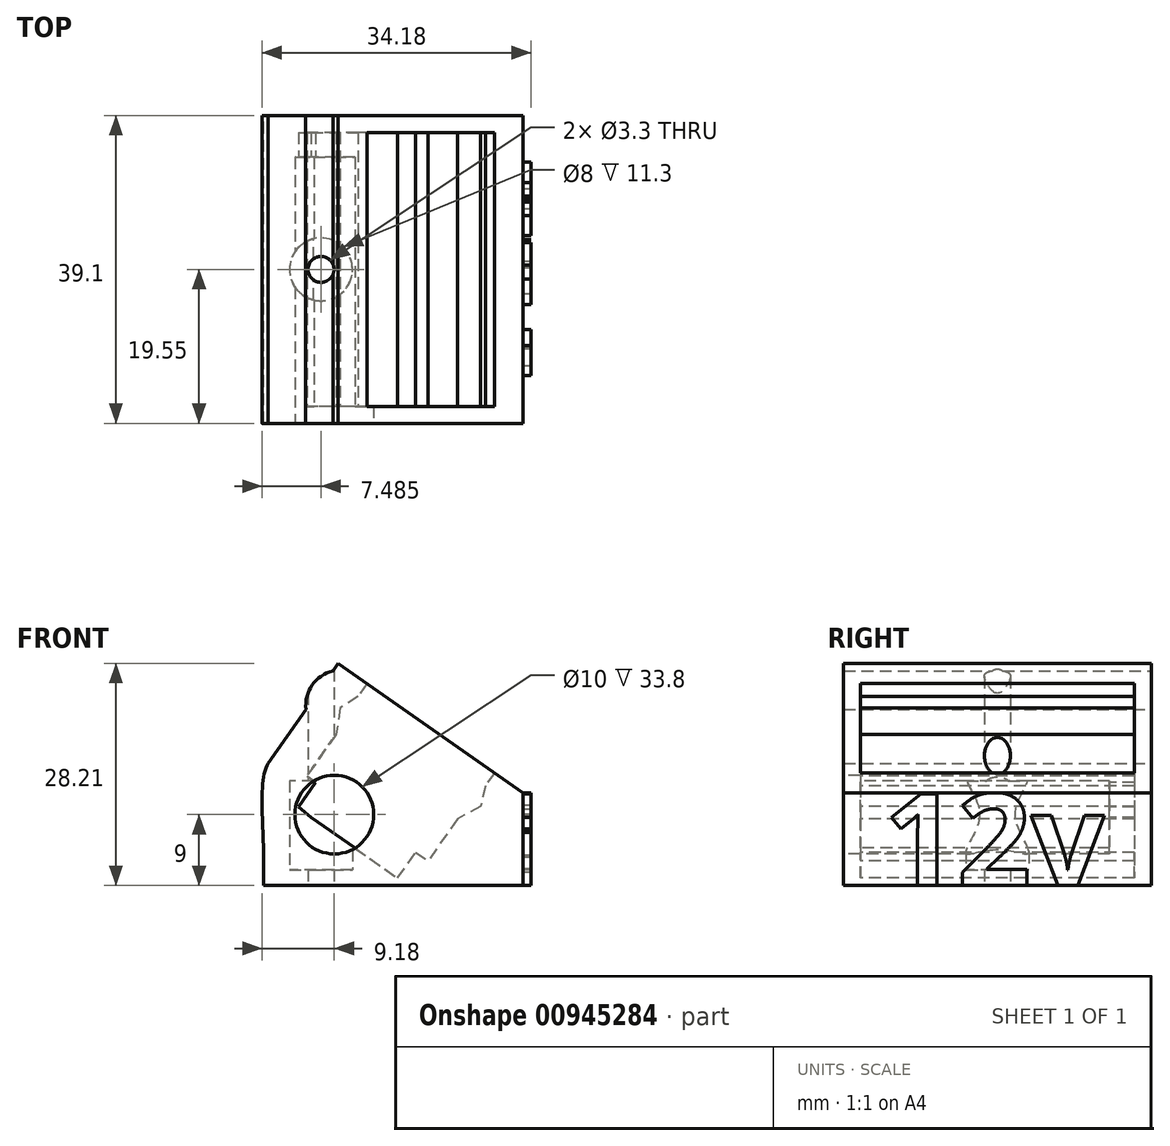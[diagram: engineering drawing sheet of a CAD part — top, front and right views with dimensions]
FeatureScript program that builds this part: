
annotation { "Feature Type Name" : "Feature", "Feature Type Description" : "" }
export const myFeature = defineFeature(function(context is Context, id is Id, definition is map)
    precondition{}
    {
        {
            var Q0;
            Q0=qCreatedBy(makeId("Front.planeOp"),FACE);
            var sketch = newSketch(context, id + "F0", { "sketchPlane" : qUnion([Q0])});
            skLineSegment(sketch, "E0.bottom", {"start": v(0, 0) * mm, "end": v(-33, 0) * mm});
            skLineSegment(sketch, "E0.top", {"start": v(0, 4) * mm, "end": v(-33, 4) * mm});
            skLineSegment(sketch, "E0.left", {"start": v(0, 0) * mm, "end": v(0, 4) * mm});
            skLineSegment(sketch, "E0.right", {"start": v(-33, 0) * mm, "end": v(-33, 4) * mm});
            skLineSegment(sketch, "E1", {"start": v(-30.88, 15.06) * mm, "end": v(-9.83, 0.32) * mm, "construction": true});
            skLineSegment(sketch, "E2", {"start": v(-9.83, 0.32) * mm, "end": v(-1.23, 12.6) * mm, "construction": true});
            skLineSegment(sketch, "E3", {"start": v(-1.23, 12.6) * mm, "end": v(0, 11.74) * mm, "construction": true});
            skLineSegment(sketch, "E4", {"start": v(-22.28, 27.35) * mm, "end": v(-30.88, 15.06) * mm, "construction": true});
            skLineSegment(sketch, "E5", {"start": v(0, 4) * mm, "end": v(0, 11.74) * mm});
            skLineSegment(sketch, "E6", {"start": v(-32.4, 15.5) * mm, "end": v(-15.96, 4) * mm});
            skLineSegment(sketch, "E7", {"start": v(0, 7.87) * mm, "end": v(13.32, 7.87) * mm});
            skLineSegment(sketch, "E8", {"start": v(13.32, 7.87) * mm, "end": v(13.32, 0) * mm});
            skLineSegment(sketch, "E9", {"start": v(13.32, 0) * mm, "end": v(0, 0) * mm});
            skLineSegment(sketch, "E10", {"start": v(21.82, 30.5) * mm, "end": v(-34.66, 30.5) * mm, "construction": true});
            skLineSegment(sketch, "E11", {"start": v(-22.28, 27.35) * mm, "end": v(-23.5, 28.2) * mm, "construction": true});
            skLineSegment(sketch, "E12", {"start": v(-23.5, 28.2) * mm, "end": v(-21.9, 30.5) * mm, "construction": true});
            skLineSegment(sketch, "E13", {"start": v(-21.9, 30.5) * mm, "end": v(1.6, 14.04) * mm, "construction": true});
            skLineSegment(sketch, "E14", {"start": v(0, 11.74) * mm, "end": v(1.6, 14.04) * mm, "construction": true});
            skLineSegment(sketch, "E15", {"start": v(-29.2, 13.88) * mm, "end": v(-31.73, 10.28) * mm, "construction": true});
            skLineSegment(sketch, "E16", {"start": v(-31.73, 10.28) * mm, "end": v(-14.04, -2.11) * mm, "construction": true});
            skLineSegment(sketch, "E17", {"start": v(-14.04, -2.11) * mm, "end": v(-11.51, 1.5) * mm, "construction": true});
            skLineSegment(sketch, "E18", {"start": v(-22.88, 4.08) * mm, "end": v(-20.36, 7.69) * mm, "construction": true});
            skLineSegment(sketch, "E19", {"start": v(0, 11.74) * mm, "end": v(-23.5, 28.2) * mm});
            skLineSegment(sketch, "E20", {"start": v(-23.5, 28.2) * mm, "end": v(-32.4, 15.5) * mm});
            skLineSegment(sketch, "E21", {"start": v(-1.1, 12.52) * mm, "end": v(-9.87, 0) * mm});
            skLineSegment(sketch, "E22", {"start": v(-22.4, 27.43) * mm, "end": v(-31.3, 14.74) * mm});
            skFitSpline(sketch, "E23", {"points": [v(-32.4, 15.5) * mm, v(-33, 4) * mm], "startDerivative": vector(-3.84, -5.87) * mm, "endDerivative": vector(0, -11.95) * mm});
            skLineSegment(sketch, "E24", {"start": v(-15.96, 4) * mm, "end": v(-10.25, 0) * mm});
            skLineSegment(sketch, "E25", {"start": v(-23.03, 26.54) * mm, "end": v(-25.92, 24.77) * mm});
            skLineSegment(sketch, "E26", {"start": v(-25.92, 24.77) * mm, "end": v(-26.47, 21.62) * mm});
            skLineSegment(sketch, "E27.MirrorCS", {"start": v(-1.73, 11.62) * mm, "end": v(-2.4, 8.3) * mm});
            skLineSegment(sketch, "E28.MirrorCS", {"start": v(-2.4, 8.3) * mm, "end": v(-5.17, 6.7) * mm});
            skArc(sketch, "E29", {"start": v(-24.18, 27.25) * mm, "mid": v(-26.8, 25.44) * mm, "end": v(-27.6, 22.35) * mm});
            skLineSegment(sketch, "E30", {"start": v(-23.25, 28.02) * mm, "end": v(-25.23, 25.19) * mm});
            skLineSegment(sketch, "E31.MirrorCS", {"start": v(-0.26, 11.93) * mm, "end": v(-2.25, 9.1) * mm});
            skLineSegment(sketch, "E32", {"start": v(-19.45, 25.37) * mm, "end": v(-27.48, 13.9) * mm});
            skLineSegment(sketch, "E33", {"start": v(-19.85, 25.64) * mm, "end": v(-21, 24) * mm});
            skLineSegment(sketch, "E34", {"start": v(-21, 24) * mm, "end": v(-23.26, 22.54) * mm});
            skLineSegment(sketch, "E35", {"start": v(-23.26, 22.54) * mm, "end": v(-23.77, 19.2) * mm});
            skLineSegment(sketch, "E36", {"start": v(-23.26, 22.54) * mm, "end": v(-22.04, 21.68) * mm});
            skLineSegment(sketch, "E37.MirrorCS", {"start": v(-4.05, 14.58) * mm, "end": v(-12.08, 3.12) * mm});
            skLineSegment(sketch, "E38.MirrorCS", {"start": v(-5.4, 10.04) * mm, "end": v(-8.37, 8.42) * mm});
            skLineSegment(sketch, "E39.MirrorCS", {"start": v(-4.8, 12.67) * mm, "end": v(-5.4, 10.04) * mm});
            skLineSegment(sketch, "E40.MirrorCS", {"start": v(-3.66, 14.3) * mm, "end": v(-4.8, 12.67) * mm});
            skLineSegment(sketch, "E41", {"start": v(-27.48, 13.9) * mm, "end": v(-12.08, 3.12) * mm});
            skLineSegment(sketch, "E42", {"start": v(-26.93, 8.63) * mm, "end": v(-18.27, 2.57) * mm});
            skLineSegment(sketch, "E43", {"start": v(-18.27, 2.57) * mm, "end": v(-15.95, 0.94) * mm});
            skLineSegment(sketch, "E44", {"start": v(-15.95, 0.94) * mm, "end": v(-13.66, 4.22) * mm});
            skLineSegment(sketch, "E45", {"start": v(-26.36, 13.11) * mm, "end": v(-28.56, 9.97) * mm});
            skLineSegment(sketch, "E46", {"start": v(-28.56, 9.97) * mm, "end": v(-26.93, 8.63) * mm});
            skSolve(sketch);
        }
        {
            var Q0;
            {var subQ6=sQuery(id+"F0.wireOp",EDGE,"E33");Q0=makeQuery(id+"F0.imprint","IMPRINT",FACE,{"disambiguationData":[TD([[makeQuery(id+"F0.imprint","IMPRINT",EDGE,{"derivedFrom":subQ6}),-1.0]])]});}
            var Q1;
            {var subQ3=sQuery(id+"F0.wireOp",EDGE,"E37.MirrorCS");var subQ4=sQuery(id+"F0.wireOp",EDGE,"E0.top");var subQ5=makeQuery(id+"F0.imprint","INTERSECT",VERTEX,{"derivedFrom":[subQ4,subQ3]});Q1=makeQuery(id+"F0.imprint","IMPRINT",FACE,{"disambiguationData":[TD([[makeQuery(id+"F0.imprint","IMPRINT",EDGE,{"disambiguationData":[TD([[subQ5,-1.0]])],"derivedFrom":subQ4}),-1.0]])]});}
            var Q2;
            {var subQ0=sQuery(id+"F0.wireOp",EDGE,"E38.MirrorCS");Q2=makeQuery(id+"F0.imprint","IMPRINT",FACE,{"disambiguationData":[TD([[makeQuery(id+"F0.imprint","IMPRINT",EDGE,{"derivedFrom":subQ0}),-1.0]])]});}
            var Q3;
            {var subQ10=sQuery(id+"F0.wireOp",EDGE,"E38.MirrorCS");Q3=makeQuery(id+"F0.imprint","IMPRINT",FACE,{"disambiguationData":[TD([[makeQuery(id+"F0.imprint","IMPRINT",EDGE,{"derivedFrom":subQ10}),1.0]])]});}
            var Q4;
            {var subQ7=sQuery(id+"F0.wireOp",EDGE,"E24");Q4=makeQuery(id+"F0.imprint","IMPRINT",FACE,{"disambiguationData":[TD([[makeQuery(id+"F0.imprint","IMPRINT",EDGE,{"derivedFrom":subQ7}),1.0]])]});}
            var Q5;
            {var subQ0=sQuery(id+"F0.wireOp",EDGE,"E37.MirrorCS");var subQ1=sQuery(id+"F0.wireOp",EDGE,"E0.top");var subQ2=makeQuery(id+"F0.imprint","INTERSECT",VERTEX,{"derivedFrom":[subQ1,subQ0]});Q5=makeQuery(id+"F0.imprint","IMPRINT",FACE,{"disambiguationData":[TD([[makeQuery(id+"F0.imprint","IMPRINT",EDGE,{"disambiguationData":[TD([[subQ2,-1.0]])],"derivedFrom":subQ1}),1.0]])]});}
            var Q6;
            {var subQ5=sQuery(id+"F0.wireOp",EDGE,"E28.MirrorCS");Q6=makeQuery(id+"F0.imprint","IMPRINT",FACE,{"disambiguationData":[TD([[makeQuery(id+"F0.imprint","IMPRINT",EDGE,{"derivedFrom":subQ5}),1.0]])]});}
            var Q7;
            {var subQ3=sQuery(id+"F0.wireOp",EDGE,"E28.MirrorCS");Q7=makeQuery(id+"F0.imprint","IMPRINT",FACE,{"disambiguationData":[TD([[makeQuery(id+"F0.imprint","IMPRINT",EDGE,{"derivedFrom":subQ3}),-1.0]])]});}
            var Q8;
            {var subQ3=sQuery(id+"F0.wireOp",EDGE,"E31.MirrorCS");Q8=makeQuery(id+"F0.imprint","IMPRINT",FACE,{"disambiguationData":[TD([[makeQuery(id+"F0.imprint","IMPRINT",EDGE,{"derivedFrom":subQ3}),-1.0]])]});}
            var Q9;
            {var subQ0=sQuery(id+"F0.wireOp",EDGE,"E0.left");Q9=makeQuery(id+"F0.imprint","IMPRINT",FACE,{"disambiguationData":[TD([[makeQuery(id+"F0.imprint","IMPRINT",EDGE,{"derivedFrom":subQ0}),1.0]])]});}
            var Q10;
            {var subQ0=sQuery(id+"F0.wireOp",EDGE,"E0.right");Q10=makeQuery(id+"F0.imprint","IMPRINT",FACE,{"disambiguationData":[TD([[makeQuery(id+"F0.imprint","IMPRINT",EDGE,{"derivedFrom":subQ0}),-1.0]])]});}
            var Q11;
            {var subQ0=sQuery(id+"F0.wireOp",EDGE,"E23");Q11=makeQuery(id+"F0.imprint","IMPRINT",FACE,{"disambiguationData":[TD([[makeQuery(id+"F0.imprint","IMPRINT",EDGE,{"derivedFrom":subQ0}),1.0]])]});}
            var Q12;
            {var subQ3=sQuery(id+"F0.wireOp",EDGE,"E26");Q12=makeQuery(id+"F0.imprint","IMPRINT",FACE,{"disambiguationData":[TD([[makeQuery(id+"F0.imprint","IMPRINT",EDGE,{"derivedFrom":subQ3}),-1.0]])]});}
            var Q13;
            {var subQ0=sQuery(id+"F0.wireOp",EDGE,"E35");Q13=makeQuery(id+"F0.imprint","IMPRINT",FACE,{"disambiguationData":[TD([[makeQuery(id+"F0.imprint","IMPRINT",EDGE,{"derivedFrom":subQ0}),1.0]])]});}
            var Q14;
            {var subQ0=sQuery(id+"F0.wireOp",EDGE,"E33");Q14=makeQuery(id+"F0.imprint","IMPRINT",FACE,{"disambiguationData":[TD([[makeQuery(id+"F0.imprint","IMPRINT",EDGE,{"derivedFrom":subQ0}),1.0]])]});}
            var Q15;
            {var subQ3=sQuery(id+"F0.wireOp",EDGE,"E26");Q15=makeQuery(id+"F0.imprint","IMPRINT",FACE,{"disambiguationData":[TD([[makeQuery(id+"F0.imprint","IMPRINT",EDGE,{"derivedFrom":subQ3}),1.0]])]});}
            var Q16;
            {var subQ3=sQuery(id+"F0.wireOp",EDGE,"E30");Q16=makeQuery(id+"F0.imprint","IMPRINT",FACE,{"disambiguationData":[TD([[makeQuery(id+"F0.imprint","IMPRINT",EDGE,{"derivedFrom":subQ3}),1.0]])]});}
            var Q17;
            {var subQ6=sQuery(id+"F0.wireOp",EDGE,"E30");Q17=makeQuery(id+"F0.imprint","IMPRINT",FACE,{"disambiguationData":[TD([[makeQuery(id+"F0.imprint","IMPRINT",EDGE,{"derivedFrom":subQ6}),-1.0]])]});}
            var Q18;
            {var subQ0=sQuery(id+"F0.wireOp",EDGE,"E44");var subQ1=sQuery(id+"F0.wireOp",EDGE,"E41");var subQ2=makeQuery(id+"F0.imprint","INTERSECT",VERTEX,{"derivedFrom":[subQ1,subQ0]});Q18=makeQuery(id+"F0.imprint","IMPRINT",FACE,{"disambiguationData":[TD([[makeQuery(id+"F0.imprint","IMPRINT",EDGE,{"disambiguationData":[TD([[subQ2,1.0]])],"derivedFrom":subQ1}),-1.0]])]});}
            var Q19;
            {var subQ0=sQuery(id+"F0.wireOp",EDGE,"E46");Q19=makeQuery(id+"F0.imprint","IMPRINT",FACE,{"disambiguationData":[TD([[makeQuery(id+"F0.imprint","IMPRINT",EDGE,{"derivedFrom":subQ0}),1.0]])]});}
            var Q20;
            {var subQ0=sQuery(id+"F0.wireOp",EDGE,"E21");var subQ5=sQuery(id+"F0.wireOp",EDGE,"E0.bottom");var subQ6=makeQuery(id+"F0.imprint","INTERSECT",VERTEX,{"derivedFrom":[subQ5,subQ0]});Q20=makeQuery(id+"F0.imprint","IMPRINT",FACE,{"disambiguationData":[TD([[makeQuery(id+"F0.imprint","IMPRINT",EDGE,{"disambiguationData":[TD([[subQ6,-1.0]])],"derivedFrom":subQ5}),-1.0]])]});}
            var Q21;
            {var subQ0=sQuery(id+"F0.wireOp",EDGE,"E41");var subQ1=sQuery(id+"F0.wireOp",EDGE,"E0.top");var subQ2=makeQuery(id+"F0.imprint","INTERSECT",VERTEX,{"derivedFrom":[subQ1,subQ0]});Q21=makeQuery(id+"F0.imprint","IMPRINT",FACE,{"disambiguationData":[TD([[makeQuery(id+"F0.imprint","IMPRINT",EDGE,{"disambiguationData":[TD([[subQ2,-1.0]])],"derivedFrom":subQ1}),-1.0]])]});}
            var Q22;
            {var subQ0=sQuery(id+"F0.wireOp",EDGE,"E43");Q22=makeQuery(id+"F0.imprint","IMPRINT",FACE,{"disambiguationData":[TD([[makeQuery(id+"F0.imprint","IMPRINT",EDGE,{"derivedFrom":subQ0}),1.0]])]});}
            var Q23;
            {var subQ2=sQuery(id+"F0.wireOp",EDGE,"E29");Q23=makeQuery(id+"F0.imprint","IMPRINT",FACE,{"disambiguationData":[TD([[makeQuery(id+"F0.imprint","IMPRINT",EDGE,{"derivedFrom":subQ2}),1.0]])]});}
            extrude(context, id + "F1", {"entities" : qUnion([Q0, Q1, Q2, Q3, Q4, Q5, Q6, Q7, Q8, Q9, Q10, Q11, Q12, Q13, Q14, Q15, Q16, Q17, Q18, Q19, Q20, Q21, Q22, Q23]), "endBound" : BoundingType.SYMMETRIC, "depth" : 39.1 * mm, "offsetDistance" : 25 * mm});
        }
        {
            var Q0;
            {var subQ0=sQuery(id+"F0.wireOp",EDGE,"E35");Q0=makeQuery(id+"F0.imprint","IMPRINT",FACE,{"disambiguationData":[TD([[makeQuery(id+"F0.imprint","IMPRINT",EDGE,{"derivedFrom":subQ0}),1.0]])]});}
            var Q1;
            {var subQ0=sQuery(id+"F0.wireOp",EDGE,"E33");Q1=makeQuery(id+"F0.imprint","IMPRINT",FACE,{"disambiguationData":[TD([[makeQuery(id+"F0.imprint","IMPRINT",EDGE,{"derivedFrom":subQ0}),1.0]])]});}
            var Q2;
            {var subQ3=sQuery(id+"F0.wireOp",EDGE,"E37.MirrorCS");var subQ4=sQuery(id+"F0.wireOp",EDGE,"E0.top");var subQ5=makeQuery(id+"F0.imprint","INTERSECT",VERTEX,{"derivedFrom":[subQ4,subQ3]});Q2=makeQuery(id+"F0.imprint","IMPRINT",FACE,{"disambiguationData":[TD([[makeQuery(id+"F0.imprint","IMPRINT",EDGE,{"disambiguationData":[TD([[subQ5,-1.0]])],"derivedFrom":subQ4}),-1.0]])]});}
            var Q3;
            {var subQ0=sQuery(id+"F0.wireOp",EDGE,"E38.MirrorCS");Q3=makeQuery(id+"F0.imprint","IMPRINT",FACE,{"disambiguationData":[TD([[makeQuery(id+"F0.imprint","IMPRINT",EDGE,{"derivedFrom":subQ0}),-1.0]])]});}
            var Q4;
            {var subQ0=sQuery(id+"F0.wireOp",EDGE,"E37.MirrorCS");var subQ1=sQuery(id+"F0.wireOp",EDGE,"E0.top");var subQ2=makeQuery(id+"F0.imprint","INTERSECT",VERTEX,{"derivedFrom":[subQ1,subQ0]});Q4=makeQuery(id+"F0.imprint","IMPRINT",FACE,{"disambiguationData":[TD([[makeQuery(id+"F0.imprint","IMPRINT",EDGE,{"disambiguationData":[TD([[subQ2,-1.0]])],"derivedFrom":subQ1}),1.0]])]});}
            var Q5;
            {var subQ0=sQuery(id+"F0.wireOp",EDGE,"E46");Q5=makeQuery(id+"F0.imprint","IMPRINT",FACE,{"disambiguationData":[TD([[makeQuery(id+"F0.imprint","IMPRINT",EDGE,{"derivedFrom":subQ0}),1.0]])]});}
            var Q6;
            {var subQ0=sQuery(id+"F0.wireOp",EDGE,"E44");var subQ1=sQuery(id+"F0.wireOp",EDGE,"E41");var subQ2=makeQuery(id+"F0.imprint","INTERSECT",VERTEX,{"derivedFrom":[subQ1,subQ0]});Q6=makeQuery(id+"F0.imprint","IMPRINT",FACE,{"disambiguationData":[TD([[makeQuery(id+"F0.imprint","IMPRINT",EDGE,{"disambiguationData":[TD([[subQ2,1.0]])],"derivedFrom":subQ1}),-1.0]])]});}
            var Q7;
            {var subQ0=sQuery(id+"F0.wireOp",EDGE,"E43");Q7=makeQuery(id+"F0.imprint","IMPRINT",FACE,{"disambiguationData":[TD([[makeQuery(id+"F0.imprint","IMPRINT",EDGE,{"derivedFrom":subQ0}),1.0]])]});}
            var Q8;
            {var subQ1=sQuery(id+"F0.wireOp",EDGE,"E0.top");var subQ3=sQuery(id+"F0.wireOp",EDGE,"E44");var subQ4=makeQuery(id+"F0.imprint","INTERSECT",VERTEX,{"derivedFrom":[subQ1,subQ3]});Q8=makeQuery(id+"F0.imprint","IMPRINT",FACE,{"disambiguationData":[TD([[makeQuery(id+"F0.imprint","IMPRINT",EDGE,{"disambiguationData":[TD([[subQ4,1.0]])],"derivedFrom":subQ3}),1.0]])]});}
            extrude(context, id + "F2", {"entities" : qUnion([Q0, Q1, Q2, Q3, Q4, Q5, Q6, Q7, Q8]), "operationType" : NewBodyOperationType.REMOVE, "endBound" : BoundingType.SYMMETRIC, "oppositeDirection" : true, "depth" : 34.8 * mm, "offsetDistance" : 25 * mm});
        }
        {
            var Q0;
            Q0=makeQuery(id+"F1.opExtrude","CAP_FACE",FACE,{"disambiguationData":[OSD([sQuery(id+"F0.wireOp",EDGE,"E0.bottom"),sQuery(id+"F0.wireOp",EDGE,"E0.left"),sQuery(id+"F0.wireOp",EDGE,"E0.right"),sQuery(id+"F0.wireOp",EDGE,"E5"),sQuery(id+"F0.wireOp",EDGE,"E19"),sQuery(id+"F0.wireOp",EDGE,"E20"),sQuery(id+"F0.wireOp",EDGE,"E23"),sQuery(id+"F0.wireOp",EDGE,"E29")])],"isStart":false});
            var sketch = newSketch(context, id + "F3", { "sketchPlane" : qUnion([Q0])});
            skCircle(sketch, "E47", {"center": v(-24, 9) * mm, "radius": 5 * mm});
            skSolve(sketch);
        }
        {
            var Q0;
            Q0=makeQuery(id+"F3.imprint","IMPRINT",FACE,{"disambiguationData":[TD([[makeQuery(id+"F3.imprint","IMPRINT",EDGE,{"derivedFrom":sQuery(id+"F3.wireOp",EDGE,"E47")}),1.0]])]});
            extrude(context, id + "F4", {"entities" : qUnion([Q0]), "operationType" : NewBodyOperationType.REMOVE, "oppositeDirection" : true, "depth" : 33.8 * mm, "offsetDistance" : 25 * mm});
        }
        {
            var Q0;
            Q0=qCreatedBy(makeId("Top.planeOp"),FACE);
            var sketch = newSketch(context, id + "F5", { "sketchPlane" : qUnion([Q0])});
            skCircle(sketch, "E48", {"center": v(-25.7, 0) * mm, "radius": 1.65 * mm});
            skCircle(sketch, "E49", {"center": v(-25.7, 0) * mm, "radius": 4 * mm});
            skSolve(sketch);
        }
        {
            var Q0;
            Q0=makeQuery(id+"F5.imprint","IMPRINT",FACE,{"disambiguationData":[TD([[makeQuery(id+"F5.imprint","IMPRINT",EDGE,{"derivedFrom":sQuery(id+"F5.wireOp",EDGE,"E48")}),1.0]])]});
            extrude(context, id + "F6", {"entities" : qUnion([Q0]), "operationType" : NewBodyOperationType.REMOVE, "depth" : 28.3 * mm, "offsetDistance" : 25 * mm});
        }
        {
            var Q0;
            Q0=makeQuery(id+"F5.imprint","IMPRINT",FACE,{"disambiguationData":[TD([[makeQuery(id+"F5.imprint","IMPRINT",EDGE,{"derivedFrom":sQuery(id+"F5.wireOp",EDGE,"E48")}),-1.0]])]});
            extrude(context, id + "F7", {"entities" : qUnion([Q0]), "operationType" : NewBodyOperationType.REMOVE, "depth" : 13.3 * mm, "offsetDistance" : 25 * mm, "hasSecondDirection" : true, "secondDirectionOppositeDirection" : false, "secondDirectionDepth" : 2 * mm});
        }
        {
            var Q0;
            Q0=makeQuery(id+"F1.opExtrude","SWEPT_FACE",FACE,{"disambiguationData":[OSD([sQuery(id+"F0.wireOp",EDGE,"E0.left"),sQuery(id+"F0.wireOp",EDGE,"E5")])]});
            var sketch = newSketch(context, id + "F8", { "sketchPlane" : qUnion([Q0])});
            skText(sketch, "E50", { "text": "12v", "fontName": "OpenSans-Bold.ttf"});
            const initialGuessF8  = {"E50": [-0.01443, -6e-05, 1, 0, 0.0118]};
            skSetInitialGuess(sketch, initialGuessF8);
            skSolve(sketch);
        }
        {
            var Q0;
            {var subQ0=sQuery(id+"F8.wireOp",EDGE,"E50.sketch_text.stroke-2");Q0=makeQuery(id+"F8.imprint","IMPRINT",FACE,{"disambiguationData":[TD([[makeQuery(id+"F8.imprint","IMPRINT",EDGE,{"derivedFrom":subQ0}),-1.0]])]});}
            var Q1;
            {var subQ7=sQuery(id+"F8.wireOp",EDGE,"E50.sketch_text.stroke-12");Q1=makeQuery(id+"F8.imprint","IMPRINT",FACE,{"disambiguationData":[TD([[makeQuery(id+"F8.imprint","IMPRINT",EDGE,{"derivedFrom":subQ7}),-1.0]])]});}
            var Q2;
            {var subQ0=sQuery(id+"F8.wireOp",EDGE,"E50.sketch_text.stroke-35");Q2=makeQuery(id+"F8.imprint","IMPRINT",FACE,{"disambiguationData":[TD([[makeQuery(id+"F8.imprint","IMPRINT",EDGE,{"derivedFrom":subQ0}),-1.0]])]});}
            extrude(context, id + "F9", {"entities" : qUnion([Q0, Q1, Q2]), "operationType" : NewBodyOperationType.ADD, "depth" : 1 * mm, "offsetDistance" : 25 * mm});
        }
    });
